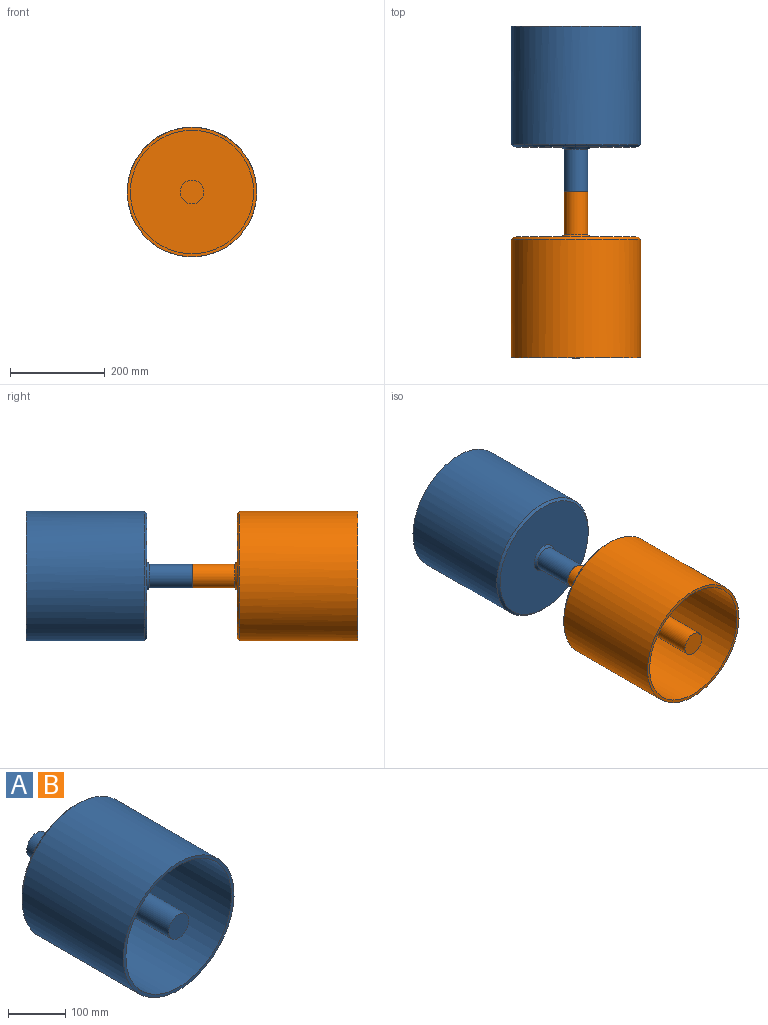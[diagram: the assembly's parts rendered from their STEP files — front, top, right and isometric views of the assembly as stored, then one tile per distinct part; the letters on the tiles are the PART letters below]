
ASSEMBLY  parts=2 mates=1
PART A: 11 faces, bbox 273x350x273 mm
  f0: cylinder r=25mm len=245mm, axis (0,1,0), area 38484.5mm2, adj f1,f2
  f1: plane 50x50mm, normal (0,-1,0), area 1963.5mm2, adj f0
  f2: plane 260.4x260.4mm, normal (0,-1,0), area 51292.9mm2, adj f0,f3
  f3: cylinder r=130.2mm len=260.4mm, axis (0,1,0), area 200427.3mm2, adj f2,f5
  f4: cylinder r=136.5mm len=273mm, axis (0,1,0), area 214413.7mm2, adj f5,f9
  f5: plane 273x273mm, normal (0,-1,0), area 5278.5mm2, adj f3,f4
  f6: plane 263x263mm, normal (0,1,0), area 51497.8mm2, adj f9,f10
  f7: plane 50x50mm, normal (0,1,0), area 1963.5mm2, adj f8
  f8: cylinder r=25mm len=90mm, axis (0,1,0), area 14137.2mm2, adj f7,f10
  f9: cone r=136.5mm half-angle=45deg, axis (0,-1,0), area 5953.5mm2, adj f4,f6
  f10: cone r=30mm half-angle=45deg, axis (0,-1,0), area 1221.8mm2, adj f6,f8
PART B: same geometry as A
PLACE A rot(axis=(1,0,0),180deg) t=(15.82,-55.55,22.71)mm
PLACE B t=(15.82,-55.55,22.71)mm
MATE revolute A.f0 <-> B.f0  axis (0,-1,0) through (15.82,-55.55,22.71)mm
